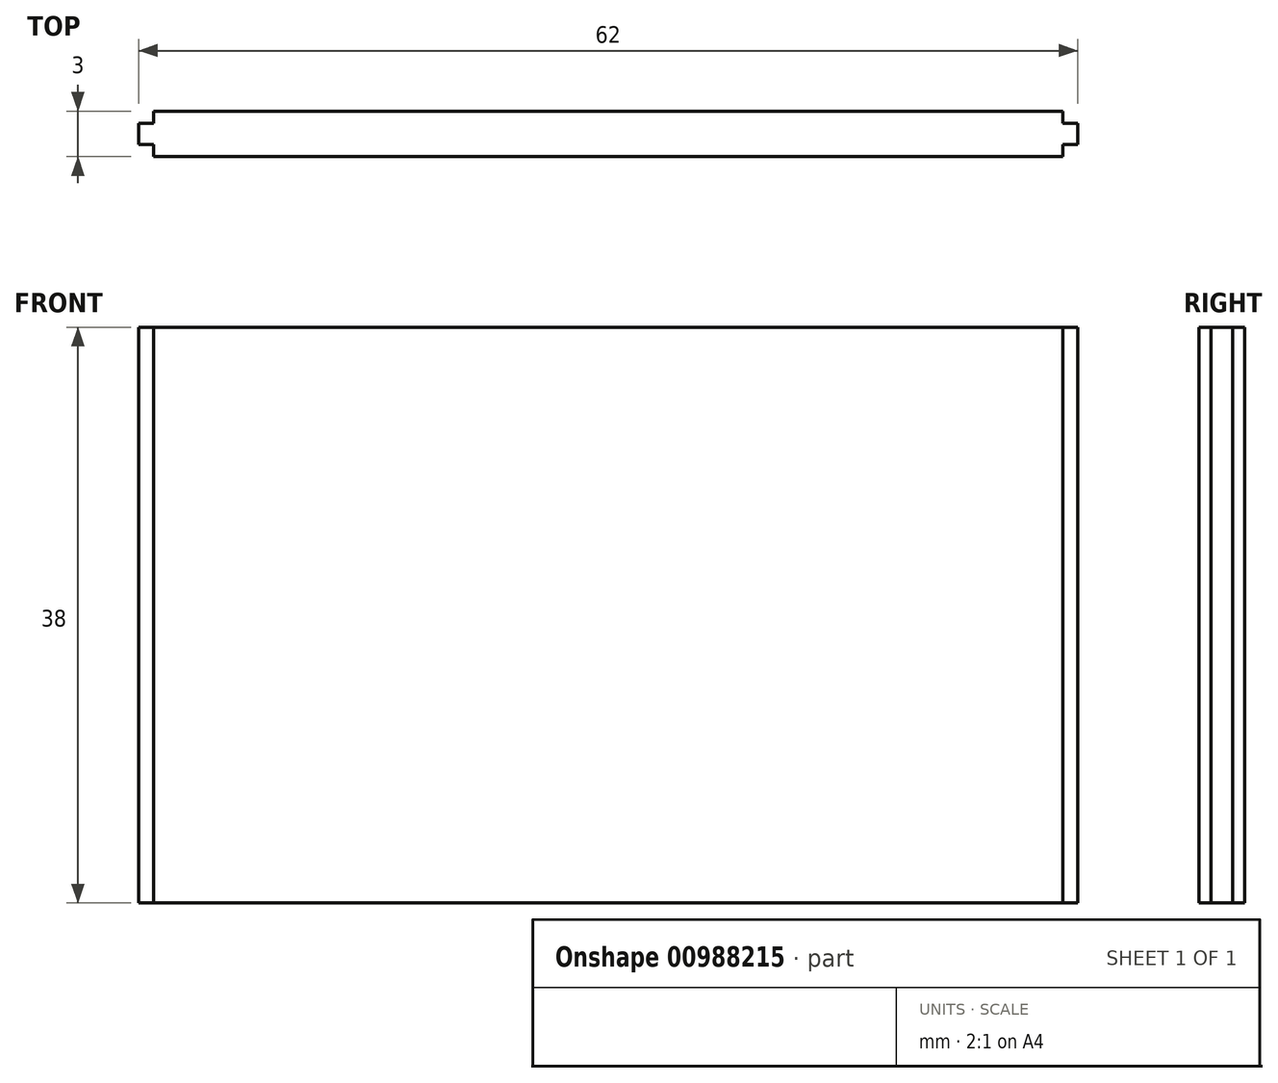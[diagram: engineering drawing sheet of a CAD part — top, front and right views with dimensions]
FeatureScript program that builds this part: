
annotation { "Feature Type Name" : "Feature", "Feature Type Description" : "" }
export const myFeature = defineFeature(function(context is Context, id is Id, definition is map)
    precondition{}
    {
        {
            var Q0;
            Q0=qCreatedBy(makeId("Top.planeOp"),FACE);
            var sketch = newSketch(context, id + "F0", { "sketchPlane" : qUnion([Q0])});
            skLineSegment(sketch, "E0.bottom", {"start": v(-30, 1.5) * mm, "end": v(30, 1.5) * mm});
            skLineSegment(sketch, "E0.top", {"start": v(-30, -1.5) * mm, "end": v(30, -1.5) * mm});
            skLineSegment(sketch, "E0.left", {"start": v(-30, 1.5) * mm, "end": v(-30, 0.7) * mm});
            skLineSegment(sketch, "E0.right", {"start": v(30, 1.5) * mm, "end": v(30, 0.7) * mm});
            skLineSegment(sketch, "E1.bottom", {"start": v(-30, 0.7) * mm, "end": v(-31, 0.7) * mm});
            skLineSegment(sketch, "E1.top", {"start": v(-30, -0.7) * mm, "end": v(-31, -0.7) * mm});
            skLineSegment(sketch, "E1.right", {"start": v(-31, 0.7) * mm, "end": v(-31, -0.7) * mm});
            skLineSegment(sketch, "E2.trimOffspring", {"start": v(-30, -0.7) * mm, "end": v(-30, -1.5) * mm});
            skLineSegment(sketch, "E3.bottom", {"start": v(30, 0.7) * mm, "end": v(31, 0.7) * mm});
            skLineSegment(sketch, "E3.top", {"start": v(30, -0.7) * mm, "end": v(31, -0.7) * mm});
            skLineSegment(sketch, "E3.right", {"start": v(31, 0.7) * mm, "end": v(31, -0.7) * mm});
            skLineSegment(sketch, "E4.trimOffspring", {"start": v(30, -0.7) * mm, "end": v(30, -1.5) * mm});
            skSolve(sketch);
        }
        {
            var Q0;
            Q0=makeQuery(id+"F0.imprint","IMPRINT",FACE,{"disambiguationData":[TD([[makeQuery(id+"F0.imprint","IMPRINT",EDGE,{"derivedFrom":sQuery(id+"F0.wireOp",EDGE,"E0.bottom")}),-1.0]])]});
            extrude(context, id + "F1", {"entities" : qUnion([Q0]), "depth" : 38 * mm, "offsetDistance" : 25 * mm});
        }
    });
